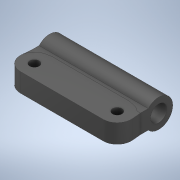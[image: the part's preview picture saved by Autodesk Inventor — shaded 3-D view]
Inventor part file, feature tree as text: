
AUTODESK INVENTOR PART (.ipt)
format: ipt  version: 2020 (Build 240168000, 168)  size: 324,608 bytes
history: native  units: in
note: dims shown in document units (in); Inventor stores cm internally (conversion verified against a paired STEP export)
features: extrude x9, sketch x9, projected_geometry x4
ambient origin geometry x8: Origin, YZ Plane, XZ Plane, XY Plane, X Axis, Y Axis, Z Axis, Center Point
bodies: Solid2 (feature_tree), Solid1 (feature_tree)
feature tree (22):
  extrude  "remove 6mm standoffs"  Depth=0.1181in
  extrude  "add 5mm left side"  Depth=0.3937in TaperAngle=0.0deg
  extrude  "add 5mm right side"  Depth=0.3937in TaperAngle=0.0deg
  extrude  "remove old chamfer"  Depth=0.3937in TaperAngle=0.0deg
  sketch  "Sketch5"  dims[d13=0.1181in d14=0.0in d15=0.1181in d16=0.0in]
  extrude  "Extrusion5"  Depth=0.1181in TaperAngle=0.0deg
  sketch  "Sketch7"
  extrude  "make standoff hole bigger"  Depth=0.2362in TaperAngle=0.0deg
  extrude  "new chamfer base"  [1 undecoded]
  extrude  "right side new chamfer"  [1 undecoded]
  extrude  "left side new chamfer"  [1 undecoded]
  sketch  "Sketch1"  dims[d0=0.1181in d1=0.1181in]
  sketch  "Sketch2"  dims[d2=0.3937in d3=0.0in d4=0.1969in d5=0.0in]
  sketch  "Sketch3"  dims[d6=0.1969in d7=0.0in d8=0.3937in d9=0.0in]
  sketch  "Sketch4"  dims[d10=0.2087in d11=0.3937in d12=0.0in]
  projected_geometry  "Projected Loop1"
  projected_geometry  "Projected Loop2"
  projected_geometry  "Projected Loop3"
  sketch  "Sketch6"  dims[d17=0.2362in d18=0.0in d19=0.2362in d20=0.0in]
  projected_geometry  "Projected Loop4"
  sketch  "Sketch9"
  sketch  "Sketch10"
note: 3 required parameter values undecoded (feature->parameter linkage not recoverable at this tier; creation-order binding heuristic only, values carry confidence <= 0.55)
